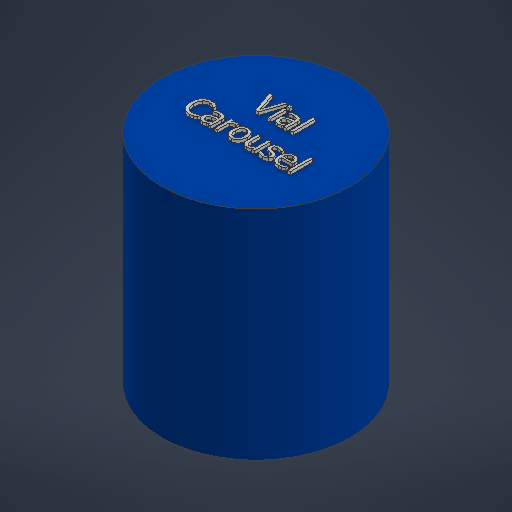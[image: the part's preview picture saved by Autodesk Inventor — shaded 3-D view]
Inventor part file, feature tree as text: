
AUTODESK INVENTOR PART (.ipt)
format: ipt  version: 2025.1 (Build 291241000, 241)  size: 457,728 bytes
history: native  units: mm
features: sketch x5, extrude x2
ambient origin geometry x8: Origin, YZ Plane, XZ Plane, XY Plane, X Axis, Y Axis, Z Axis, Center Point
bodies: Solid1 (feature_tree)
feature tree (7):
  extrude  "Extrusion1"  Depth=150.0mm TaperAngle=0.0deg
  extrude  "Extrusion2"  Depth=25.0mm
  sketch  "Sketch1"  dims[d0=130.0mm d1=150.0mm d2=0.0mm]
  sketch  "Sketch2"  dims[d6=23.0mm]
  sketch  "Sketch Circular Pattern1"  dims[d3=2.0mm d4=0.0mm d5=25.0mm]
  sketch  "Sketch Circular Pattern2"  dims[d7=60.0mm d9=360.0deg]
  sketch  "Sketch Circular Pattern3"  dims[d11=23.0mm d13=150.0deg d14=60.0mm d16=360.0deg d18=25.0mm d19=25.0mm d20=25.0mm d21=25.0mm d22=23.0mm d23=60.0mm d25=360.0deg]
